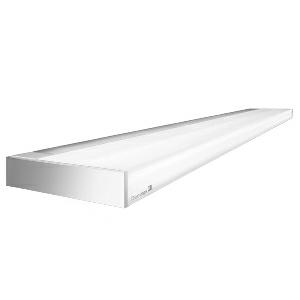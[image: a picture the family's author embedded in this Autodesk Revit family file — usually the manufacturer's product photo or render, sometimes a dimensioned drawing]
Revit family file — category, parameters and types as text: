
# Revit family: vanera_bed_-_vaw_8000_830_00812228_92a8
name_source: partatom
category: Lighting Fixtures
units: mm (PartAtom-declared; Revit-internal decimal feet)

## family parameters
Cut with Voids When Loaded = No
Host = Face
Light Source = No
Part Type = Normal
Room Calculation Point = No
Round Connector Dimension = Use Diameter
Shared = No

## types (1)
- AL+LL (1 x LED, 7500 lm, 3000K)
    Apparent Load = 71 VA
    Approval mark = CE
    CIE Flux Codes = 46 76 94 28 100
    Color Rendering = 80-89
    Color Temperature = 3000K
    Control Gear = Electronic ballast
    Default Elevation = 2000 mm  [stored 6.56168 ft]
    Description = VAW 8000/830|Wall-mounted luminaire|light source:   Warm white   |work equipment: Power supply unit|luminous flux: 7500 lm|light distribution: Direct/indirect|class of protection: I|technology: Two-stage switchable|mains lead: Connection box 3 pin|glare control: Diffusor|special features: General light, indirect, 3000K, Ra80, DIN EN 60598-2-25, Reading light, direct, 3,00K, Ra80, Protective low voltage relay (LVC)|
    Frequency = 50 Hz, 60 Hz
    Height = 45 mm
    Lamp = 1 x LED
    Lamp Light Flux = 7500 lm
    Lamp count = 1
    Length = 1200 mm
    Luminous efficacy = 106 lm/W
    Manufacturer = Waldmann
    ModVariant = No
    Model = 00812228
    Mounting Place = Wall
    Mounting Type = Surface mounted
    Number of Poles = 1
    OnlyDefault = Yes
    Power Factor = 1
    Product Name = VANERA.bed - VAW 8000/830
    Product group = Wall mounted Luminaire
    ProductGroupID = 20
    Protection Class = Protection class I
    Protection Degree = Degree of protection
    RLX_Detail_Level = 1
    RLX_Emergency_Light_Flux = 0 lm
    RLX_Emergency_Type = 0
    RLX_Emergency_Type_DB = No
    RlxData = <blob elided: 63045 chars, md5=9b9d1d2c>
    Socket = socket
    Standby Power = 0 W
    System Light Flux = 7500 lm
    System Power = 71 W
    Type Comments = Allgemeinlicht und Leselicht
    Type Image = vanera_opal_54_54_w.jpg
    URL = http://relux.com
    VarID = al_ll_67c3
    Voltage = 230 V
    Voltage Range = 220-240 V
    Weight = 0.00 kg
    Width = 160 mm

note: [stored X ft] marks values corroborated as IEEE doubles in the binary element streams (Revit-internal decimal feet)

## geometry (parser evidence)
native form markers: Blend x4, Sweep x13
no freeform markers — native parametric forms only
